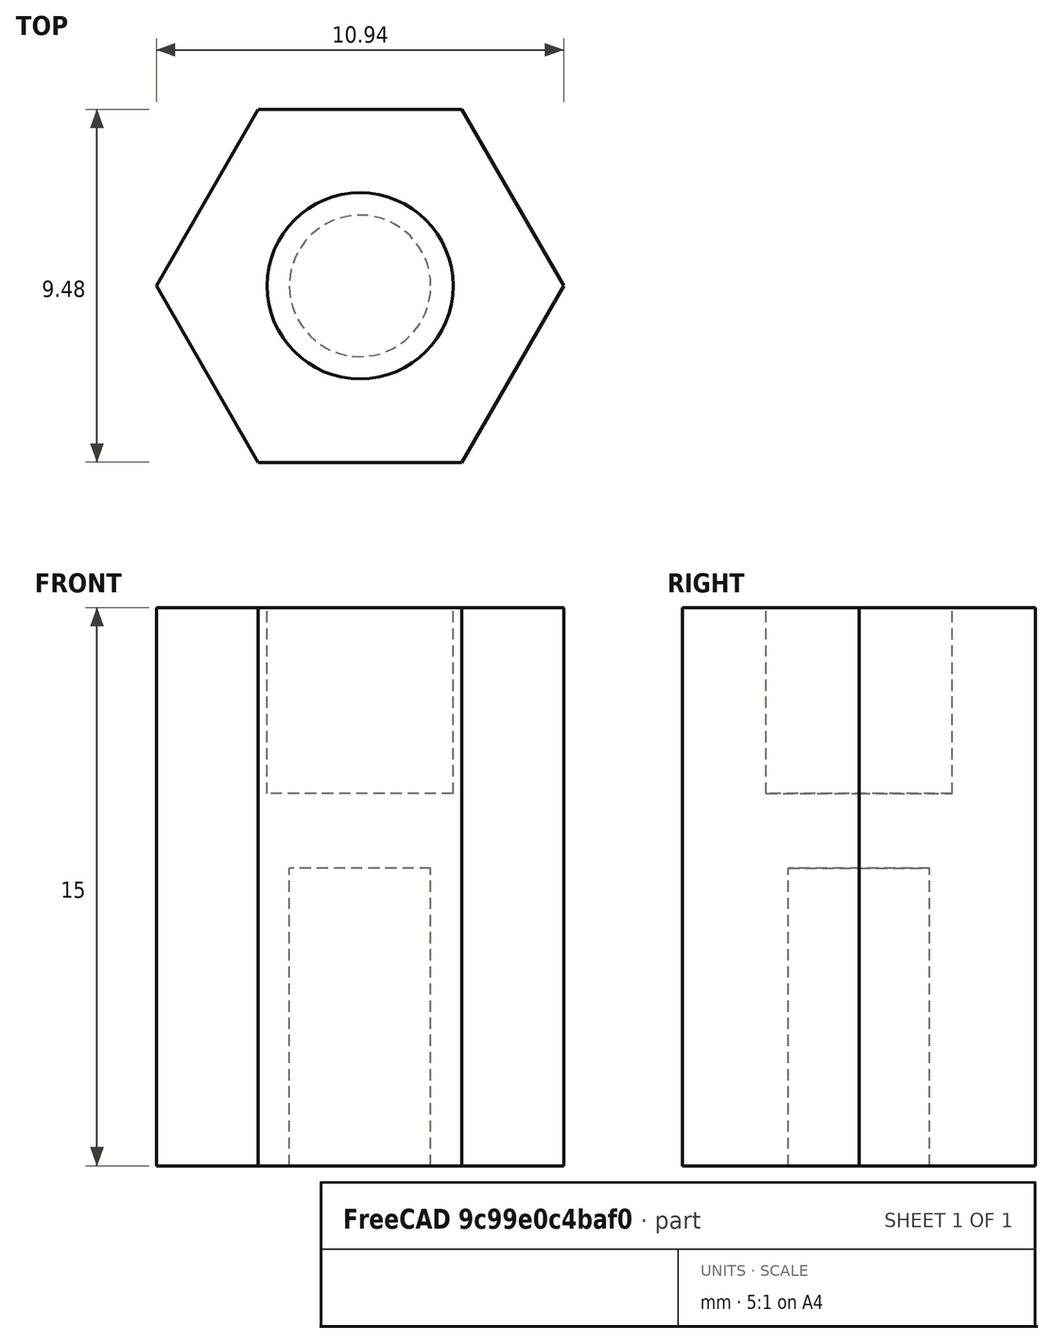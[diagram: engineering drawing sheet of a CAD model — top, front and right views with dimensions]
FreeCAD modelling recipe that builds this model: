
FCSTD DOCUMENT  (FreeCAD 0.17R13541 (Git))
Label: tip-changer-shaft-fixer
License: All rights reserved
LicenseURL: http://en.wikipedia.org/wiki/All_rights_reserved
objects: Spreadsheet::Sheet×2, Part::Cylinder×2, Part::Cut×2, Part::Prism×1, Mesh::Feature×1
note: 5 computed .brp shape members not serialized (recipe doc carries the construction recipe); baked Part::Feature solids carry a one-line shape summary decoded from their .brp

FEATURE [Spreadsheet::Sheet] Spreadsheet
  cells = A1=steigung; B1=h; D1(pitch)=1.5; F1=bauhöhe; G1(height)=20; A2=Gewindetiefe; B2=t; C2=h*cos(30°); D2(threaddepth)==pitch * cos(30); F2=helix height; G2(height_h)=25; C3=threaddepth tol; D3(threaddepth_tol)==(pitch + tolerance * cos(30)) * cos(30); F3=Flanken - Tolerance; G3(tolerance)=0; A4=Nut; F4=Radien - Tolerance; G4(tolerance_rad)=0.20000000000000001; A5=ra; E5(nut_ra)==bolt_ri + bolt_si + threaddepth + nut_sa; A6=sa; E6(nut_sa)=3; A7=ri; E7(nut_ri)==nb_centerline - threaddepth / 2 + threaddepth / 4 + tolerance_rad; A9=Bolt; A10=ri; E10(bolt_ri)==E16; A11=si; E11(bolt_si)==E17; G11==sqrt(1 / 6 ^ 2 - (tan(30) / 4) ^ 2) * Spreadsheet.threaddepth_tol; A12=ra; E12(bolt_ra)==nb_centerline + threaddepth / 2 - threaddepth / 8 - tolerance_rad; A14=Nut/Bold centerline; E14(nb_centerline)==bolt_ri + bolt_si + threaddepth / 2; A16=Spring rh; E16(spring_rh)==Tabelle1.B18 / 2 + Tabelle1.B3; A17=hülsenstärke sh; E17(spring_sh)==Tabelle1.B19; A18=join rest   js; E18(spring_sj)=1.3999999999999999; A21=join heigtht jh; B21(spring_jh)=3; A22=join ri; B22(spring_jri)==spring_rh + spring_sh + tolerance
FEATURE [Part::Cylinder] Cylinder022  label="Zylinder020"
  Angle = 360
  AttacherType = Attacher::AttachEngine3D
  Height = 5
  Placement = pos=(0,0,10) rot=(0,0,1;0rad)
  Radius = 2.5
FEATURE [Part::Prism] Prism  label="Prisma"
  AttacherType = Attacher::AttachEngine3D
  Circumradius = 5.47476
  Height = 15
  Polygon = 6
  expr: Circumradius = Spreadsheet.nut_ri - 0.050000000000000003
FEATURE [Part::Cut] Cut039
  Base = -> Prism
  Tool = -> Cylinder022
FEATURE [Part::Cylinder] Cylinder017  label="Zylinder017"
  Angle = 360
  AttacherType = Attacher::AttachEngine3D
  Height = 8
  Radius = 1.9
FEATURE [Part::Cut] Cut040  label="tip-changer-shaft-fixer"
  Base = -> Cut039
  Placement = pos=(0,0,18) rot=(0,0,1;0rad)
  Tool = -> Cylinder017
FEATURE [Spreadsheet::Sheet] Tabelle1
  cells = A1=Abstand Pip/Boden; B1=65; A3=Toleranz; B3=0.20000000000000001; A5=Teller; A6=Breite/Länge; B6=65; A7=Dicke; B7=5; A8=Befestigung höhe; B8=10; A10=Achse; A11=Durchmesser; B11=5; A12=Teller Befestigung; B12==B7 + B8; A13=Führung Länge; B13=40; C13=Wandstärke; D13=5; A14=Freiraum; B14=5; A15=Länge; B15==B14 + B13 + B12; A17=Feder; A18=Hülse durchmesser; B18=3.6000000000000001; A19=Hülse Wanddicke; B19=3; A20=L0; B20=25; A21=delta L; B21=3; A22=Spannmutter; A23=Höhe; B23=10; A24=Durchmesser Pitch; B24=20; A25=min Abstand Boden; B25=5; A28=min Oberkante Platte; B28==B25 + B23 + B20 + B19 + B13 + B7; A30=Gehäuse; A31=Wandstärke; B31=5; A32=Durchmesser; B32==B24 + 2 * B31; A33=Höhe; B33==B25 + B20 + B19 + B13; A35=Spitze d1; B35=7; A36=Spitze d2; B36=6.5; A37=Raster; B37=10.5; A38=Anzahl x/y; B38=6; A39=offset; B39==(Tabelle1.B6 - ((Tabelle1.B38 - 1) * Tabelle1.B37 + Tabelle1.B35)) / 2 + Tabelle1.B35 / 2
FEATURE [Mesh::Feature] Mesh  label="tip-changer-shaft-fixer (Meshed)"
